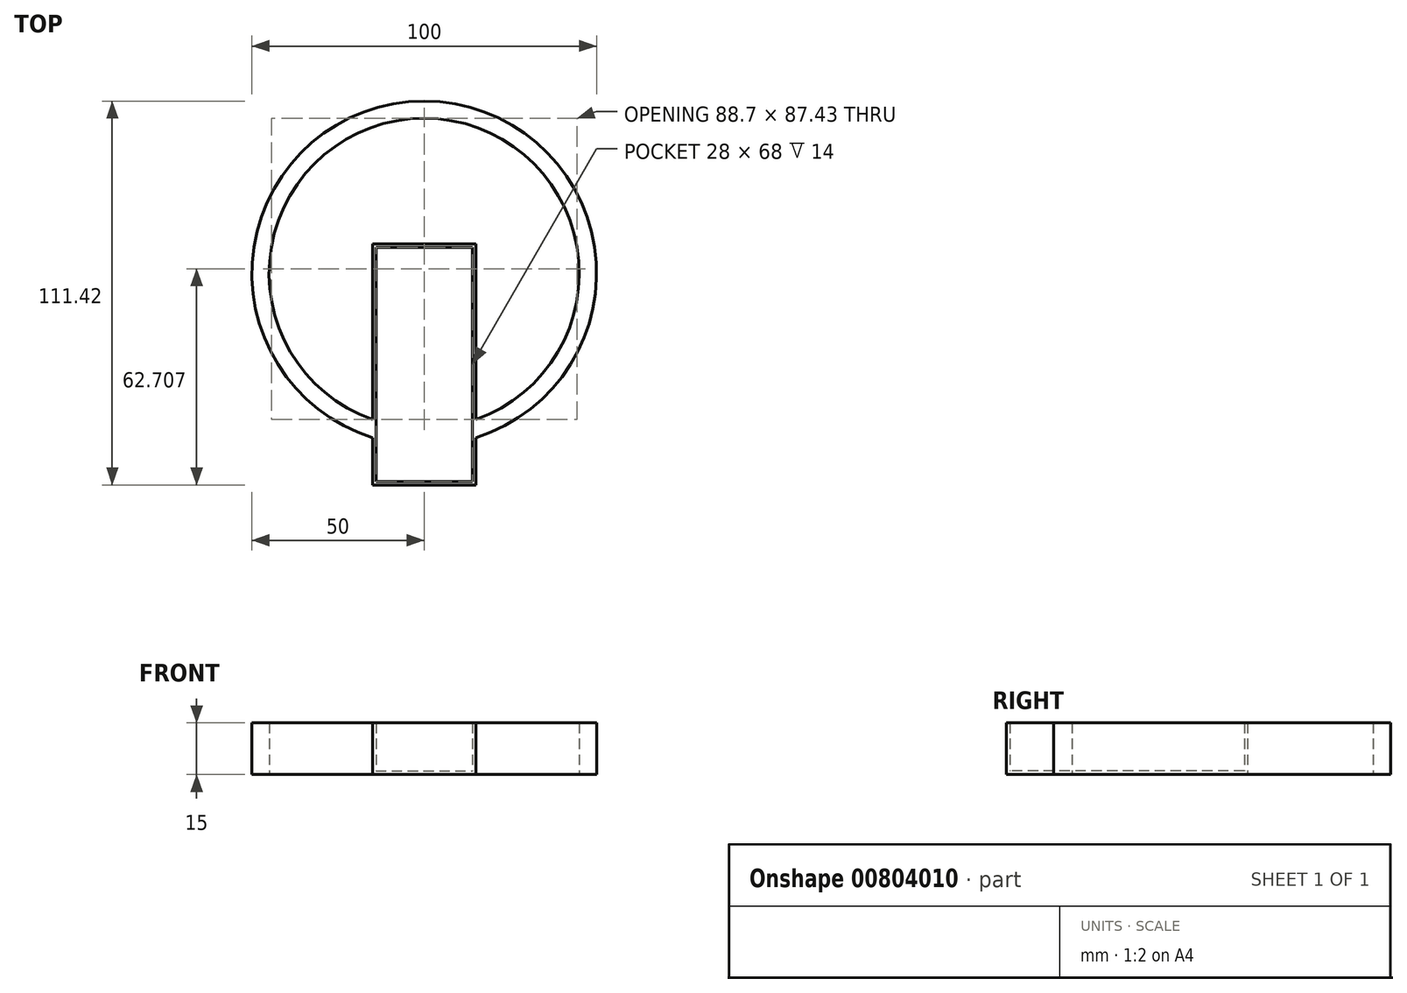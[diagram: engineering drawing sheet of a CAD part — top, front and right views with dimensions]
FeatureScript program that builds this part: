
annotation { "Feature Type Name" : "Feature", "Feature Type Description" : "" }
export const myFeature = defineFeature(function(context is Context, id is Id, definition is map)
    precondition{}
    {
        {
            var Q0;
            Q0=qCreatedBy(makeId("Top.planeOp"),FACE);
            var sketch = newSketch(context, id + "F0", { "sketchPlane" : qUnion([Q0])});
            skCircle(sketch, "E0", {"center": v(0, 0) * mm, "radius": 50 * mm});
            skCircle(sketch, "E1", {"center": v(0, 0) * mm, "radius": 45 * mm});
            skSolve(sketch);
        }
        {
            var Q0;
            Q0=makeQuery(id+"F0.imprint","IMPRINT",FACE,{"disambiguationData":[TD([[makeQuery(id+"F0.imprint","IMPRINT",EDGE,{"derivedFrom":sQuery(id+"F0.wireOp",EDGE,"E0")}),1.0]])]});
            extrude(context, id + "F1", {"entities" : qUnion([Q0]), "depth" : 15 * mm, "offsetDistance" : 25 * mm});
        }
        {
            var Q0;
            Q0=qCreatedBy(makeId("Front.planeOp"),FACE);
            var sketch = newSketch(context, id + "F2", { "sketchPlane" : qUnion([Q0])});
            skLineSegment(sketch, "E2.bottom", {"start": v(15, 0) * mm, "end": v(-15, 0) * mm});
            skLineSegment(sketch, "E2.top", {"start": v(15, 15) * mm, "end": v(-15, 15) * mm});
            skLineSegment(sketch, "E2.left", {"start": v(15, 0) * mm, "end": v(15, 15) * mm});
            skLineSegment(sketch, "E2.right", {"start": v(-15, 0) * mm, "end": v(-15, 15) * mm});
            skSolve(sketch);
        }
        {
            var Q0;
            Q0=makeQuery(id+"F2.imprint","IMPRINT",FACE,{"disambiguationData":[TD([[makeQuery(id+"F2.imprint","IMPRINT",EDGE,{"derivedFrom":sQuery(id+"F2.wireOp",EDGE,"E2.bottom")}),-1.0]])]});
            extrude(context, id + "F3", {"entities" : qUnion([Q0]), "operationType" : NewBodyOperationType.REMOVE, "depth" : 50 * mm, "offsetDistance" : 25 * mm});
        }
        {
            var Q0;
            Q0=qCreatedBy(makeId("Top.planeOp"),FACE);
            var sketch = newSketch(context, id + "F4", { "sketchPlane" : qUnion([Q0])});
            skLineSegment(sketch, "E3.bottom", {"start": v(-15, 8.58) * mm, "end": v(15, 8.58) * mm});
            skLineSegment(sketch, "E3.top", {"start": v(-15, -61.42) * mm, "end": v(15, -61.42) * mm});
            skLineSegment(sketch, "E3.left", {"start": v(-15, 8.58) * mm, "end": v(-15, -61.42) * mm});
            skLineSegment(sketch, "E3.right", {"start": v(15, 8.58) * mm, "end": v(15, -61.42) * mm});
            skPoint(sketch, "E3.middle", {"position": v(0, -26.42) * mm});
            skSolve(sketch);
        }
        {
            var Q0;
            Q0=makeQuery(id+"F4.imprint","IMPRINT",FACE,{"disambiguationData":[TD([[makeQuery(id+"F4.imprint","IMPRINT",EDGE,{"derivedFrom":sQuery(id+"F4.wireOp",EDGE,"E3.bottom")}),-1.0]])]});
            var sketch = newSketch(context, id + "F5", { "sketchPlane" : qUnion([Q0])});
            skLineSegment(sketch, "E4.bottom", {"start": v(-14, 7.58) * mm, "end": v(14, 7.58) * mm});
            skLineSegment(sketch, "E4.top", {"start": v(-14, -60.42) * mm, "end": v(14, -60.42) * mm});
            skLineSegment(sketch, "E4.left", {"start": v(-14, 7.58) * mm, "end": v(-14, -60.42) * mm});
            skLineSegment(sketch, "E4.right", {"start": v(14, 7.58) * mm, "end": v(14, -60.42) * mm});
            skPoint(sketch, "E4.middle", {"position": v(0, -26.42) * mm});
            skSolve(sketch);
        }
        {
            var Q0;
            Q0=makeQuery(id+"F5.imprint","IMPRINT",FACE,{"disambiguationData":[TD([[makeQuery(id+"F5.imprint","IMPRINT",EDGE,{"derivedFrom":sQuery(id+"F5.wireOp",EDGE,"E4.bottom")}),1.0]])]});
            extrude(context, id + "F6", {"entities" : qUnion([Q0]), "operationType" : NewBodyOperationType.ADD, "depth" : 15 * mm, "offsetDistance" : 25 * mm});
        }
        {
            var Q0;
            Q0=qCreatedBy(makeId("Top.planeOp"),FACE);
            var sketch = newSketch(context, id + "F7", { "sketchPlane" : qUnion([Q0])});
            skLineSegment(sketch, "E5.bottom", {"start": v(-14, 7.58) * mm, "end": v(14, 7.58) * mm});
            skLineSegment(sketch, "E5.top", {"start": v(-14, -60.42) * mm, "end": v(14, -60.42) * mm});
            skLineSegment(sketch, "E5.left", {"start": v(-14, 7.58) * mm, "end": v(-14, -60.42) * mm});
            skLineSegment(sketch, "E5.right", {"start": v(14, 7.58) * mm, "end": v(14, -60.42) * mm});
            skPoint(sketch, "E5.middle", {"position": v(0, -26.42) * mm});
            skSolve(sketch);
        }
        {
            var Q0;
            Q0=makeQuery(id+"F7.imprint","IMPRINT",FACE,{"disambiguationData":[TD([[makeQuery(id+"F7.imprint","IMPRINT",EDGE,{"derivedFrom":sQuery(id+"F7.wireOp",EDGE,"E5.bottom")}),-1.0]])]});
            extrude(context, id + "F8", {"entities" : qUnion([Q0]), "operationType" : NewBodyOperationType.ADD, "depth" : 1 * mm, "offsetDistance" : 25 * mm});
        }
    });
